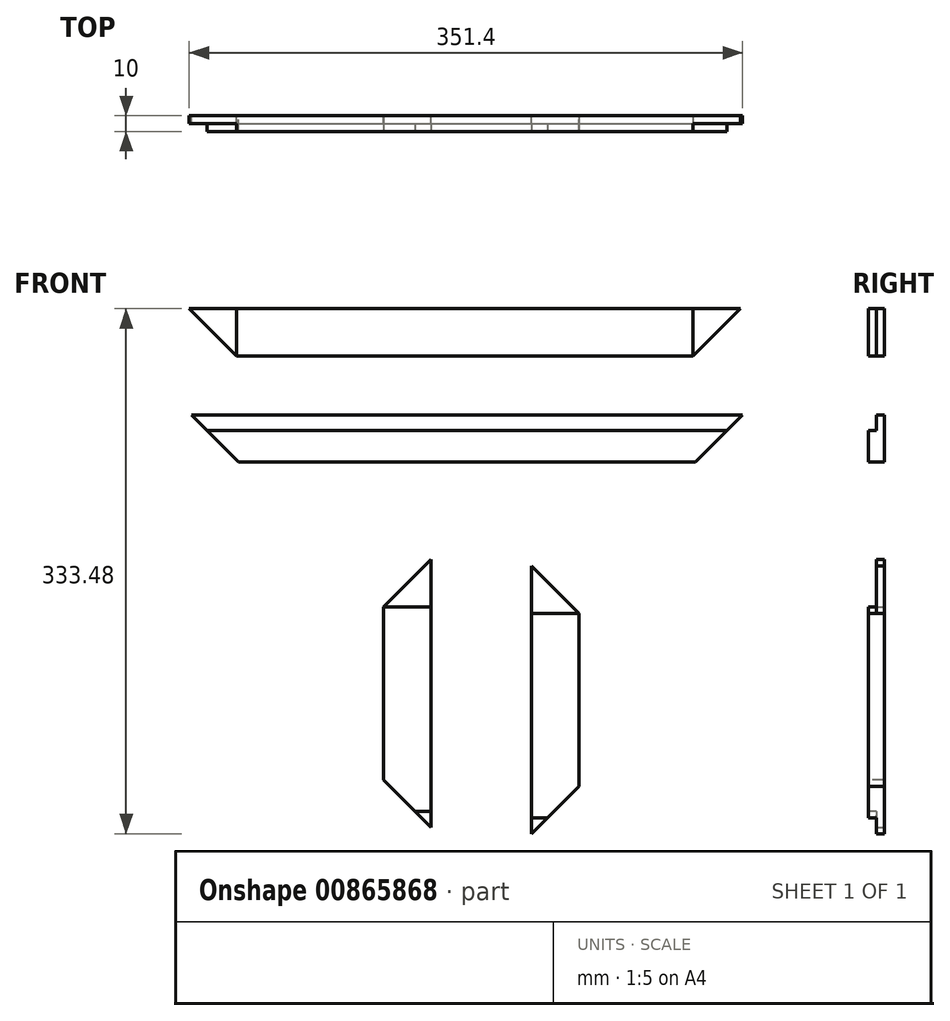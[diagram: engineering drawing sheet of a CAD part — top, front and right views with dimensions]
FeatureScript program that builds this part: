
annotation { "Feature Type Name" : "Feature", "Feature Type Description" : "" }
export const myFeature = defineFeature(function(context is Context, id is Id, definition is map)
    precondition{}
    {
        {
            var Q0;
            Q0=qCreatedBy(makeId("Front.planeOp"),FACE);
            var sketch = newSketch(context, id + "F0", { "sketchPlane" : qUnion([Q0])});
            skLineSegment(sketch, "E0.bottom", {"start": v(-196.62, 121.3) * mm, "end": v(153.38, 121.3) * mm});
            skLineSegment(sketch, "E0.top", {"start": v(-196.62, 91.3) * mm, "end": v(153.38, 91.3) * mm});
            skLineSegment(sketch, "E0.left", {"start": v(-196.62, 121.3) * mm, "end": v(-196.62, 91.3) * mm});
            skLineSegment(sketch, "E0.right", {"start": v(153.38, 121.3) * mm, "end": v(153.38, 91.3) * mm});
            skLineSegment(sketch, "E1.bottom", {"start": v(-73.21, -38) * mm, "end": v(-43.21, -38) * mm});
            skLineSegment(sketch, "E1.top", {"start": v(-73.21, -208) * mm, "end": v(-43.21, -208) * mm});
            skLineSegment(sketch, "E1.left", {"start": v(-73.21, -38) * mm, "end": v(-73.21, -208) * mm});
            skLineSegment(sketch, "E1.right", {"start": v(-43.21, -38) * mm, "end": v(-43.21, -208) * mm});
            skLineSegment(sketch, "E2.bottom", {"start": v(20.8, -42.17) * mm, "end": v(50.8, -42.17) * mm});
            skLineSegment(sketch, "E2.top", {"start": v(20.8, -212.17) * mm, "end": v(50.8, -212.17) * mm});
            skLineSegment(sketch, "E2.left", {"start": v(20.8, -42.17) * mm, "end": v(20.8, -212.17) * mm});
            skLineSegment(sketch, "E2.right", {"start": v(50.8, -42.17) * mm, "end": v(50.8, -212.17) * mm});
            skSolve(sketch);
        }
        {
            var Q0;
            Q0 = qSketchRegion(id + "F0", true);
            extrude(context, id + "F1", {"entities" : qUnion([Q0]), "depth" : 10 * mm, "offsetDistance" : 25 * mm});
        }
        {
            var Q0;
            Q0=makeQuery(id+"F1.opExtrude","CAP_FACE",FACE,{"disambiguationData":[OSD([sQuery(id+"F0.wireOp",EDGE,"E0.bottom"),sQuery(id+"F0.wireOp",EDGE,"E0.top"),sQuery(id+"F0.wireOp",EDGE,"E0.left"),sQuery(id+"F0.wireOp",EDGE,"E0.right")])],"isStart":false});
            var sketch = newSketch(context, id + "F2", { "sketchPlane" : qUnion([Q0])});
            skLineSegment(sketch, "E3.bottom", {"start": v(-196.62, 121.3) * mm, "end": v(-166.62, 121.3) * mm});
            skLineSegment(sketch, "E3.top", {"start": v(-196.62, 91.3) * mm, "end": v(-166.62, 91.3) * mm});
            skLineSegment(sketch, "E3.left", {"start": v(-196.62, 121.3) * mm, "end": v(-196.62, 91.3) * mm});
            skLineSegment(sketch, "E3.right", {"start": v(-166.62, 121.3) * mm, "end": v(-166.62, 91.3) * mm});
            skLineSegment(sketch, "E4.bottom", {"start": v(153.38, 121.3) * mm, "end": v(123.38, 121.3) * mm});
            skLineSegment(sketch, "E4.top", {"start": v(153.38, 91.3) * mm, "end": v(123.38, 91.3) * mm});
            skLineSegment(sketch, "E4.left", {"start": v(153.38, 121.3) * mm, "end": v(153.38, 91.3) * mm});
            skLineSegment(sketch, "E4.right", {"start": v(123.38, 121.3) * mm, "end": v(123.38, 91.3) * mm});
            skSolve(sketch);
        }
        {
            var Q0;
            Q0 = qSketchRegion(id + "F2", true);
            extrude(context, id + "F3", {"entities" : qUnion([Q0]), "operationType" : NewBodyOperationType.REMOVE, "oppositeDirection" : true, "depth" : 5 * mm, "offsetDistance" : 25 * mm});
        }
        {
            var Q0;
            Q0=makeQuery(id+"F1.opExtrude","CAP_FACE",FACE,{"disambiguationData":[OSD([sQuery(id+"F0.wireOp",EDGE,"E1.bottom"),sQuery(id+"F0.wireOp",EDGE,"E1.top"),sQuery(id+"F0.wireOp",EDGE,"E1.left"),sQuery(id+"F0.wireOp",EDGE,"E1.right")])],"isStart":false});
            var sketch = newSketch(context, id + "F4", { "sketchPlane" : qUnion([Q0])});
            skLineSegment(sketch, "E5.bottom", {"start": v(-73.21, -38) * mm, "end": v(-43.21, -38) * mm});
            skLineSegment(sketch, "E5.top", {"start": v(-73.21, -68) * mm, "end": v(-43.21, -68) * mm});
            skLineSegment(sketch, "E5.left", {"start": v(-73.21, -38) * mm, "end": v(-73.21, -68) * mm});
            skLineSegment(sketch, "E5.right", {"start": v(-43.21, -38) * mm, "end": v(-43.21, -68) * mm});
            skLineSegment(sketch, "E6.bottom", {"start": v(-73.21, -208) * mm, "end": v(-43.21, -208) * mm});
            skLineSegment(sketch, "E6.top", {"start": v(-73.21, -198) * mm, "end": v(-43.21, -198) * mm});
            skLineSegment(sketch, "E6.left", {"start": v(-73.21, -208) * mm, "end": v(-73.21, -198) * mm});
            skLineSegment(sketch, "E6.right", {"start": v(-43.21, -208) * mm, "end": v(-43.21, -198) * mm});
            skSolve(sketch);
        }
        {
            var Q0;
            Q0 = qSketchRegion(id + "F4", true);
            extrude(context, id + "F5", {"entities" : qUnion([Q0]), "operationType" : NewBodyOperationType.REMOVE, "oppositeDirection" : true, "depth" : 5 * mm, "offsetDistance" : 25 * mm});
        }
        {
            var Q0;
            Q0=makeQuery(id+"F1.opExtrude","CAP_FACE",FACE,{"disambiguationData":[OSD([sQuery(id+"F0.wireOp",EDGE,"E2.bottom"),sQuery(id+"F0.wireOp",EDGE,"E2.top"),sQuery(id+"F0.wireOp",EDGE,"E2.left"),sQuery(id+"F0.wireOp",EDGE,"E2.right")])],"isStart":false});
            var sketch = newSketch(context, id + "F6", { "sketchPlane" : qUnion([Q0])});
            skLineSegment(sketch, "E7.bottom", {"start": v(20.8, -42.17) * mm, "end": v(50.8, -42.17) * mm});
            skLineSegment(sketch, "E7.top", {"start": v(20.8, -72.17) * mm, "end": v(50.8, -72.17) * mm});
            skLineSegment(sketch, "E7.left", {"start": v(20.8, -42.17) * mm, "end": v(20.8, -72.17) * mm});
            skLineSegment(sketch, "E7.right", {"start": v(50.8, -42.17) * mm, "end": v(50.8, -72.17) * mm});
            skLineSegment(sketch, "E8.bottom", {"start": v(20.8, -212.17) * mm, "end": v(50.8, -212.17) * mm});
            skLineSegment(sketch, "E8.top", {"start": v(20.8, -202.17) * mm, "end": v(50.8, -202.17) * mm});
            skLineSegment(sketch, "E8.left", {"start": v(20.8, -212.17) * mm, "end": v(20.8, -202.17) * mm});
            skLineSegment(sketch, "E8.right", {"start": v(50.8, -212.17) * mm, "end": v(50.8, -202.17) * mm});
            skSolve(sketch);
        }
        {
            var Q0;
            Q0 = qSketchRegion(id + "F6", true);
            extrude(context, id + "F7", {"entities" : qUnion([Q0]), "operationType" : NewBodyOperationType.REMOVE, "oppositeDirection" : true, "depth" : 5 * mm, "offsetDistance" : 25 * mm});
        }
        {
            var Q0;
            Q0=qCreatedBy(makeId("Front.planeOp"),FACE);
            var sketch = newSketch(context, id + "F8", { "sketchPlane" : qUnion([Q0])});
            skLineSegment(sketch, "E9.bottom", {"start": v(-195.22, 53.86) * mm, "end": v(154.78, 53.86) * mm});
            skLineSegment(sketch, "E9.top", {"start": v(-195.22, 23.86) * mm, "end": v(154.78, 23.86) * mm});
            skLineSegment(sketch, "E9.left", {"start": v(-195.22, 53.86) * mm, "end": v(-195.22, 23.86) * mm});
            skLineSegment(sketch, "E9.right", {"start": v(154.78, 53.86) * mm, "end": v(154.78, 23.86) * mm});
            skSolve(sketch);
        }
        {
            var Q0;
            Q0 = qSketchRegion(id + "F8", true);
            extrude(context, id + "F9", {"entities" : qUnion([Q0]), "depth" : 5 * mm, "offsetDistance" : 25 * mm});
        }
        {
            var Q0;
            Q0=makeQuery(id+"F9.opExtrude","CAP_FACE",FACE,{"disambiguationData":[OSD([sQuery(id+"F8.wireOp",EDGE,"E9.bottom"),sQuery(id+"F8.wireOp",EDGE,"E9.top"),sQuery(id+"F8.wireOp",EDGE,"E9.left"),sQuery(id+"F8.wireOp",EDGE,"E9.right")])],"isStart":false});
            var sketch = newSketch(context, id + "F10", { "sketchPlane" : qUnion([Q0])});
            skLineSegment(sketch, "E10.bottom", {"start": v(-195.22, 43.86) * mm, "end": v(154.78, 43.86) * mm});
            skLineSegment(sketch, "E10.top", {"start": v(-195.22, 23.86) * mm, "end": v(154.78, 23.86) * mm});
            skLineSegment(sketch, "E10.left", {"start": v(-195.22, 43.86) * mm, "end": v(-195.22, 23.86) * mm});
            skLineSegment(sketch, "E10.right", {"start": v(154.78, 43.86) * mm, "end": v(154.78, 23.86) * mm});
            skSolve(sketch);
        }
        {
            var Q0;
            Q0 = qSketchRegion(id + "F10", true);
            extrude(context, id + "F11", {"entities" : qUnion([Q0]), "operationType" : NewBodyOperationType.ADD, "depth" : 5 * mm, "offsetDistance" : 25 * mm});
        }
        {
            var Q0;
            Q0=makeQuery(id+"F1.opExtrude","SWEPT_EDGE",EDGE,{"disambiguationData":[OSD([sQuery(id+"F0.wireOp",EDGE,"E0.top"),sQuery(id+"F0.wireOp",EDGE,"E0.left")])]});
            var Q1;
            Q1=makeQuery(id+"F1.opExtrude","SWEPT_EDGE",EDGE,{"disambiguationData":[OSD([sQuery(id+"F0.wireOp",EDGE,"E2.bottom"),sQuery(id+"F0.wireOp",EDGE,"E2.right")])]});
            var Q2;
            Q2=makeQuery(id+"F1.opExtrude","SWEPT_EDGE",EDGE,{"disambiguationData":[OSD([sQuery(id+"F0.wireOp",EDGE,"E1.bottom"),sQuery(id+"F0.wireOp",EDGE,"E1.left")])]});
            var Q3;
            Q3=makeQuery(id+"F1.opExtrude","SWEPT_EDGE",EDGE,{"disambiguationData":[OSD([sQuery(id+"F0.wireOp",EDGE,"E1.top"),sQuery(id+"F0.wireOp",EDGE,"E1.left")])]});
            var Q4;
            Q4=makeQuery(id+"F1.opExtrude","SWEPT_EDGE",EDGE,{"disambiguationData":[OSD([sQuery(id+"F0.wireOp",EDGE,"E2.top"),sQuery(id+"F0.wireOp",EDGE,"E2.right")])]});
            var Q5;
            Q5=makeQuery(id+"F1.opExtrude","SWEPT_EDGE",EDGE,{"disambiguationData":[OSD([sQuery(id+"F0.wireOp",EDGE,"E0.top"),sQuery(id+"F0.wireOp",EDGE,"E0.right")])]});
            var Q6;
            Q6=makeQuery(id+"F11.boolean.opBoolean","MERGE",EDGE,{"derivedFrom":[makeQuery(id+"F9.opExtrude","SWEPT_EDGE",EDGE,{"disambiguationData":[OSD([sQuery(id+"F8.wireOp",EDGE,"E9.top"),sQuery(id+"F8.wireOp",EDGE,"E9.left")])]}),makeQuery(id+"F11.opExtrude","SWEPT_EDGE",EDGE,{"disambiguationData":[OSD([sQuery(id+"F10.wireOp",EDGE,"E10.top"),sQuery(id+"F10.wireOp",EDGE,"E10.left")])]})]});
            var Q7;
            Q7=makeQuery(id+"F11.boolean.opBoolean","MERGE",EDGE,{"derivedFrom":[makeQuery(id+"F9.opExtrude","SWEPT_EDGE",EDGE,{"disambiguationData":[OSD([sQuery(id+"F8.wireOp",EDGE,"E9.top"),sQuery(id+"F8.wireOp",EDGE,"E9.right")])]}),makeQuery(id+"F11.opExtrude","SWEPT_EDGE",EDGE,{"disambiguationData":[OSD([sQuery(id+"F10.wireOp",EDGE,"E10.top"),sQuery(id+"F10.wireOp",EDGE,"E10.right")])]})]});
            chamfer(context, id + "F12", {"entities" : qUnion([Q0, Q1, Q2, Q3, Q4, Q5, Q6, Q7]), "width" : 30 * mm, "tangentPropagation" : true});
        }
    });
